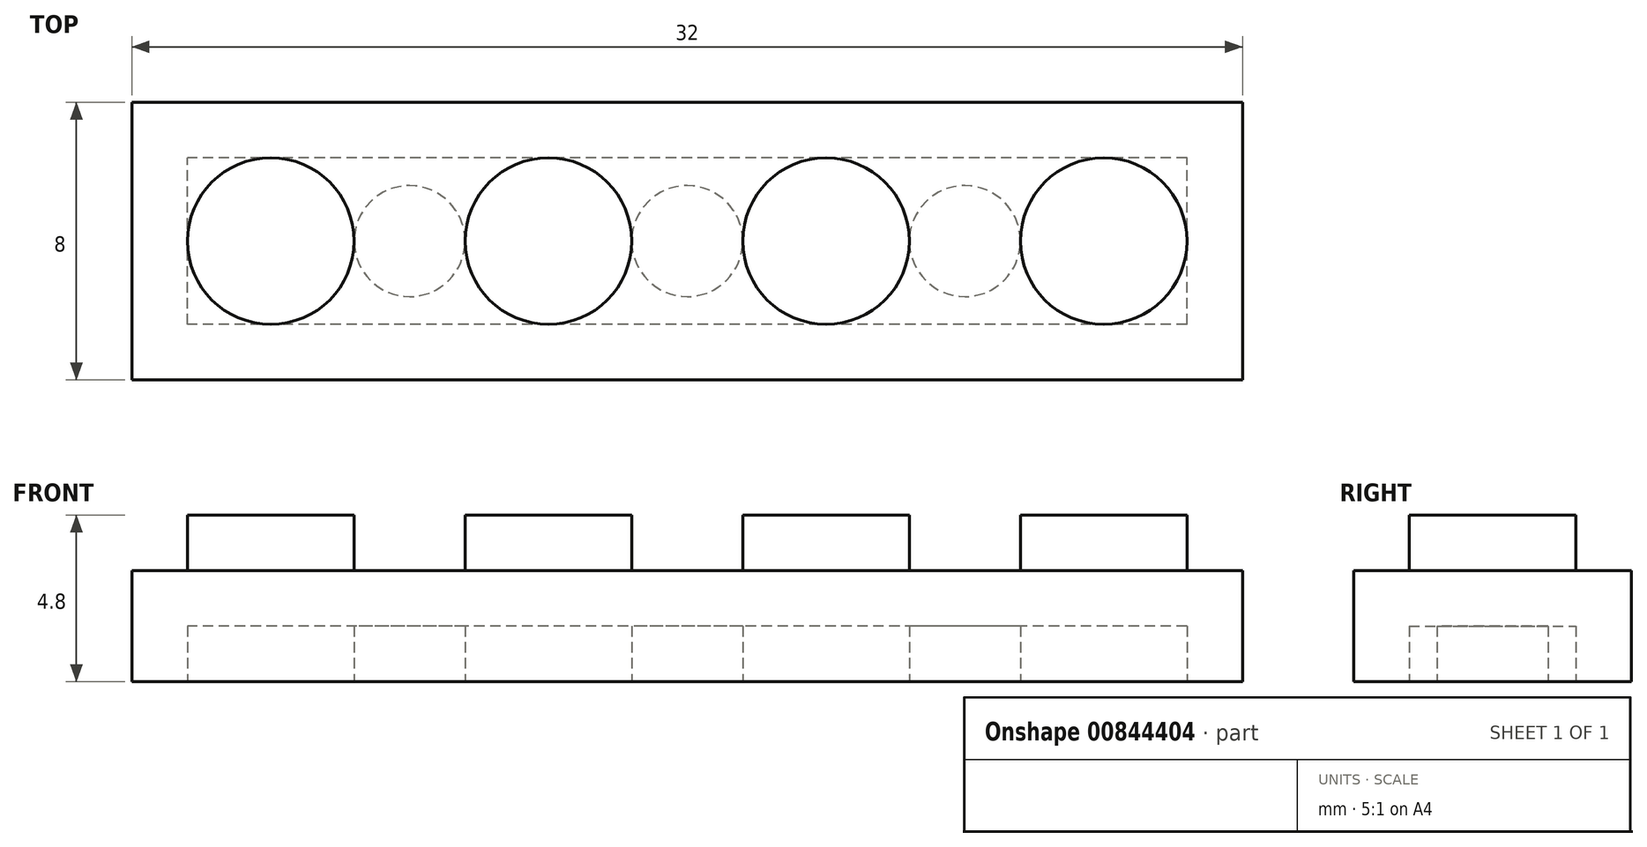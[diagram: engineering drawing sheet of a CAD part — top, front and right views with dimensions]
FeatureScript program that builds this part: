
annotation { "Feature Type Name" : "Feature", "Feature Type Description" : "" }
export const myFeature = defineFeature(function(context is Context, id is Id, definition is map)
    precondition{}
    {
        {
            var Q0;
            Q0=qCreatedBy(makeId("Top.planeOp"),FACE);
            var sketch = newSketch(context, id + "F0", { "sketchPlane" : qUnion([Q0])});
            skLineSegment(sketch, "E0.bottom", {"start": v(16, -4) * mm, "end": v(-16, -4) * mm});
            skLineSegment(sketch, "E0.top", {"start": v(16, 4) * mm, "end": v(-16, 4) * mm});
            skLineSegment(sketch, "E0.left", {"start": v(16, -4) * mm, "end": v(16, 4) * mm});
            skLineSegment(sketch, "E0.right", {"start": v(-16, -4) * mm, "end": v(-16, 4) * mm});
            skPoint(sketch, "E0.middle", {"position": v(0, 0) * mm});
            skCircle(sketch, "E1", {"center": v(-12, 0) * mm, "radius": 2.4 * mm});
            skCircle(sketch, "E2", {"center": v(-12, 0) * mm, "radius": 1.6 * mm});
            skCircle(sketch, "E3.1.0.0", {"center": v(-4, 0) * mm, "radius": 2.4 * mm});
            skCircle(sketch, "E3.2.0.0", {"center": v(4, 0) * mm, "radius": 2.4 * mm});
            skCircle(sketch, "E3.3.0.0", {"center": v(12, 0) * mm, "radius": 2.4 * mm});
            skLineSegment(sketch, "E3.direction1", {"start": v(-12, 0) * mm, "end": v(-4, 0) * mm, "construction": true});
            skCircle(sketch, "E4.1.0.0", {"center": v(-8, 0) * mm, "radius": 1.6 * mm});
            skCircle(sketch, "E4.2.0.0", {"center": v(-4, 0) * mm, "radius": 1.6 * mm});
            skCircle(sketch, "E4.3.0.0", {"center": v(0, 0) * mm, "radius": 1.6 * mm});
            skCircle(sketch, "E4.4.0.0", {"center": v(4, 0) * mm, "radius": 1.6 * mm});
            skCircle(sketch, "E4.5.0.0", {"center": v(8, 0) * mm, "radius": 1.6 * mm});
            skCircle(sketch, "E4.6.0.0", {"center": v(12, 0) * mm, "radius": 1.6 * mm});
            skLineSegment(sketch, "E4.direction1", {"start": v(-12, 0) * mm, "end": v(-8, 0) * mm, "construction": true});
            skSolve(sketch);
        }
        {
            var Q0;
            Q0=makeQuery(id+"F0.imprint","IMPRINT",FACE,{"disambiguationData":[TD([[makeQuery(id+"F0.imprint","IMPRINT",EDGE,{"derivedFrom":sQuery(id+"F0.wireOp",EDGE,"E2")}),1.0]])]});
            var Q1;
            Q1=makeQuery(id+"F0.imprint","IMPRINT",FACE,{"disambiguationData":[TD([[makeQuery(id+"F0.imprint","IMPRINT",EDGE,{"derivedFrom":sQuery(id+"F0.wireOp",EDGE,"E1")}),1.0]])]});
            var Q2;
            {var subQ0=sQuery(id+"F0.wireOp",EDGE,"E4.1.0.0");var subQ1=makeQuery(id+"F0.imprint","INTERSECT",VERTEX,{"derivedFrom":[sQuery(id+"F0.wireOp",EDGE,"E1"),subQ0]});Q2=makeQuery(id+"F0.imprint","IMPRINT",FACE,{"disambiguationData":[TD([[makeQuery(id+"F0.imprint","IMPRINT",EDGE,{"disambiguationData":[TD([[subQ1,1.0]])],"derivedFrom":subQ0}),1.0]])]});}
            var Q3;
            Q3=makeQuery(id+"F0.imprint","IMPRINT",FACE,{"disambiguationData":[TD([[makeQuery(id+"F0.imprint","IMPRINT",EDGE,{"derivedFrom":sQuery(id+"F0.wireOp",EDGE,"E4.2.0.0")}),1.0]])]});
            var Q4;
            Q4=makeQuery(id+"F0.imprint","IMPRINT",FACE,{"disambiguationData":[TD([[makeQuery(id+"F0.imprint","IMPRINT",EDGE,{"derivedFrom":sQuery(id+"F0.wireOp",EDGE,"E4.2.0.0")}),-1.0]])]});
            var Q5;
            {var subQ0=sQuery(id+"F0.wireOp",EDGE,"E4.3.0.0");var subQ1=makeQuery(id+"F0.imprint","INTERSECT",VERTEX,{"derivedFrom":[sQuery(id+"F0.wireOp",EDGE,"E3.1.0.0"),subQ0]});Q5=makeQuery(id+"F0.imprint","IMPRINT",FACE,{"disambiguationData":[TD([[makeQuery(id+"F0.imprint","IMPRINT",EDGE,{"disambiguationData":[TD([[subQ1,1.0]])],"derivedFrom":subQ0}),1.0]])]});}
            var Q6;
            Q6=makeQuery(id+"F0.imprint","IMPRINT",FACE,{"disambiguationData":[TD([[makeQuery(id+"F0.imprint","IMPRINT",EDGE,{"derivedFrom":sQuery(id+"F0.wireOp",EDGE,"E4.4.0.0")}),-1.0]])]});
            var Q7;
            Q7=makeQuery(id+"F0.imprint","IMPRINT",FACE,{"disambiguationData":[TD([[makeQuery(id+"F0.imprint","IMPRINT",EDGE,{"derivedFrom":sQuery(id+"F0.wireOp",EDGE,"E4.4.0.0")}),1.0]])]});
            var Q8;
            {var subQ0=sQuery(id+"F0.wireOp",EDGE,"E4.5.0.0");var subQ1=makeQuery(id+"F0.imprint","INTERSECT",VERTEX,{"derivedFrom":[sQuery(id+"F0.wireOp",EDGE,"E3.2.0.0"),subQ0]});Q8=makeQuery(id+"F0.imprint","IMPRINT",FACE,{"disambiguationData":[TD([[makeQuery(id+"F0.imprint","IMPRINT",EDGE,{"disambiguationData":[TD([[subQ1,1.0]])],"derivedFrom":subQ0}),1.0]])]});}
            var Q9;
            Q9=makeQuery(id+"F0.imprint","IMPRINT",FACE,{"disambiguationData":[TD([[makeQuery(id+"F0.imprint","IMPRINT",EDGE,{"derivedFrom":sQuery(id+"F0.wireOp",EDGE,"E4.6.0.0")}),1.0]])]});
            var Q10;
            Q10=makeQuery(id+"F0.imprint","IMPRINT",FACE,{"disambiguationData":[TD([[makeQuery(id+"F0.imprint","IMPRINT",EDGE,{"derivedFrom":sQuery(id+"F0.wireOp",EDGE,"E3.3.0.0")}),1.0]])]});
            var Q11;
            Q11=makeQuery(id+"F0.imprint","IMPRINT",FACE,{"disambiguationData":[TD([[makeQuery(id+"F0.imprint","IMPRINT",EDGE,{"derivedFrom":sQuery(id+"F0.wireOp",EDGE,"E0.bottom")}),-1.0]])]});
            extrude(context, id + "F1", {"entities" : qUnion([Q0, Q1, Q2, Q3, Q4, Q5, Q6, Q7, Q8, Q9, Q10, Q11]), "depth" : 3.2 * mm, "offsetDistance" : 25 * mm});
        }
        {
            var Q0;
            Q0=makeQuery(id+"F1.opExtrude","CAP_FACE",FACE,{"disambiguationData":[OSD([sQuery(id+"F0.wireOp",EDGE,"E0.bottom"),sQuery(id+"F0.wireOp",EDGE,"E0.top"),sQuery(id+"F0.wireOp",EDGE,"E0.left"),sQuery(id+"F0.wireOp",EDGE,"E0.right")])],"isStart":true});
            shell(context, id + "F2", {"entities" : qUnion([Q0]), "thickness" : 1.6 * mm});
        }
        {
            var Q0;
            {var subQ0=sQuery(id+"F0.wireOp",EDGE,"E4.1.0.0");var subQ1=makeQuery(id+"F0.imprint","INTERSECT",VERTEX,{"derivedFrom":[sQuery(id+"F0.wireOp",EDGE,"E1"),subQ0]});Q0=makeQuery(id+"F0.imprint","IMPRINT",FACE,{"disambiguationData":[TD([[makeQuery(id+"F0.imprint","IMPRINT",EDGE,{"disambiguationData":[TD([[subQ1,1.0]])],"derivedFrom":subQ0}),1.0]])]});}
            var Q1;
            {var subQ0=sQuery(id+"F0.wireOp",EDGE,"E4.3.0.0");var subQ1=makeQuery(id+"F0.imprint","INTERSECT",VERTEX,{"derivedFrom":[sQuery(id+"F0.wireOp",EDGE,"E3.1.0.0"),subQ0]});Q1=makeQuery(id+"F0.imprint","IMPRINT",FACE,{"disambiguationData":[TD([[makeQuery(id+"F0.imprint","IMPRINT",EDGE,{"disambiguationData":[TD([[subQ1,1.0]])],"derivedFrom":subQ0}),1.0]])]});}
            var Q2;
            {var subQ0=sQuery(id+"F0.wireOp",EDGE,"E4.5.0.0");var subQ1=makeQuery(id+"F0.imprint","INTERSECT",VERTEX,{"derivedFrom":[sQuery(id+"F0.wireOp",EDGE,"E3.2.0.0"),subQ0]});Q2=makeQuery(id+"F0.imprint","IMPRINT",FACE,{"disambiguationData":[TD([[makeQuery(id+"F0.imprint","IMPRINT",EDGE,{"disambiguationData":[TD([[subQ1,1.0]])],"derivedFrom":subQ0}),1.0]])]});}
            var Q3;
            Q3=makeQuery(id+"F2.opShell","OFFSET_FACE",FACE,{"disambiguationData":[OSD([sQuery(id+"F0.wireOp",EDGE,"E0.bottom"),sQuery(id+"F0.wireOp",EDGE,"E0.top"),sQuery(id+"F0.wireOp",EDGE,"E0.left"),sQuery(id+"F0.wireOp",EDGE,"E0.right")])]});
            extrude(context, id + "F3", {"entities" : qUnion([Q0, Q1, Q2]), "operationType" : NewBodyOperationType.ADD, "endBound" : BoundingType.UP_TO_SURFACE, "depth" : 25 * mm, "endBoundEntityFace" : qUnion([Q3]), "offsetDistance" : 25 * mm});
        }
        {
            var Q0;
            Q0=makeQuery(id+"F0.imprint","IMPRINT",FACE,{"disambiguationData":[TD([[makeQuery(id+"F0.imprint","IMPRINT",EDGE,{"derivedFrom":sQuery(id+"F0.wireOp",EDGE,"E1")}),1.0]])]});
            var Q1;
            Q1=makeQuery(id+"F0.imprint","IMPRINT",FACE,{"disambiguationData":[TD([[makeQuery(id+"F0.imprint","IMPRINT",EDGE,{"derivedFrom":sQuery(id+"F0.wireOp",EDGE,"E4.2.0.0")}),-1.0]])]});
            var Q2;
            Q2=makeQuery(id+"F0.imprint","IMPRINT",FACE,{"disambiguationData":[TD([[makeQuery(id+"F0.imprint","IMPRINT",EDGE,{"derivedFrom":sQuery(id+"F0.wireOp",EDGE,"E4.4.0.0")}),-1.0]])]});
            var Q3;
            Q3=makeQuery(id+"F0.imprint","IMPRINT",FACE,{"disambiguationData":[TD([[makeQuery(id+"F0.imprint","IMPRINT",EDGE,{"derivedFrom":sQuery(id+"F0.wireOp",EDGE,"E3.3.0.0")}),1.0]])]});
            var Q4;
            Q4=makeQuery(id+"F0.imprint","IMPRINT",FACE,{"disambiguationData":[TD([[makeQuery(id+"F0.imprint","IMPRINT",EDGE,{"derivedFrom":sQuery(id+"F0.wireOp",EDGE,"E2")}),1.0]])]});
            var Q5;
            Q5=makeQuery(id+"F0.imprint","IMPRINT",FACE,{"disambiguationData":[TD([[makeQuery(id+"F0.imprint","IMPRINT",EDGE,{"derivedFrom":sQuery(id+"F0.wireOp",EDGE,"E4.2.0.0")}),1.0]])]});
            var Q6;
            Q6=makeQuery(id+"F0.imprint","IMPRINT",FACE,{"disambiguationData":[TD([[makeQuery(id+"F0.imprint","IMPRINT",EDGE,{"derivedFrom":sQuery(id+"F0.wireOp",EDGE,"E4.4.0.0")}),1.0]])]});
            var Q7;
            Q7=makeQuery(id+"F0.imprint","IMPRINT",FACE,{"disambiguationData":[TD([[makeQuery(id+"F0.imprint","IMPRINT",EDGE,{"derivedFrom":sQuery(id+"F0.wireOp",EDGE,"E4.6.0.0")}),1.0]])]});
            var Q8;
            Q8=makeQuery(id+"F1.opExtrude","CAP_FACE",FACE,{"disambiguationData":[OSD([sQuery(id+"F0.wireOp",EDGE,"E0.bottom"),sQuery(id+"F0.wireOp",EDGE,"E0.top"),sQuery(id+"F0.wireOp",EDGE,"E0.left"),sQuery(id+"F0.wireOp",EDGE,"E0.right")])],"isStart":false});
            var Q9;
            Q9=makeQuery(id+"F1.opExtrude","CAP_FACE",FACE,{"disambiguationData":[OSD([sQuery(id+"F0.wireOp",EDGE,"E0.bottom"),sQuery(id+"F0.wireOp",EDGE,"E0.top"),sQuery(id+"F0.wireOp",EDGE,"E0.left"),sQuery(id+"F0.wireOp",EDGE,"E0.right")])],"isStart":false});
            extrude(context, id + "F4", {"entities" : qUnion([Q0, Q1, Q2, Q3, Q4, Q5, Q6, Q7]), "operationType" : NewBodyOperationType.ADD, "endBound" : BoundingType.UP_TO_SURFACE, "depth" : 26.1 * mm, "endBoundEntityFace" : qUnion([Q8]), "hasOffset" : true, "offsetDistance" : 1.6 * mm, "offsetOppositeDirection" : true, "hasSecondDirection" : true, "secondDirectionBound" : SecondDirectionBoundingType.UP_TO_SURFACE, "secondDirectionOppositeDirection" : false, "secondDirectionDepth" : 25 * mm, "secondDirectionBoundEntityFace" : qUnion([Q9])});
        }
    });
